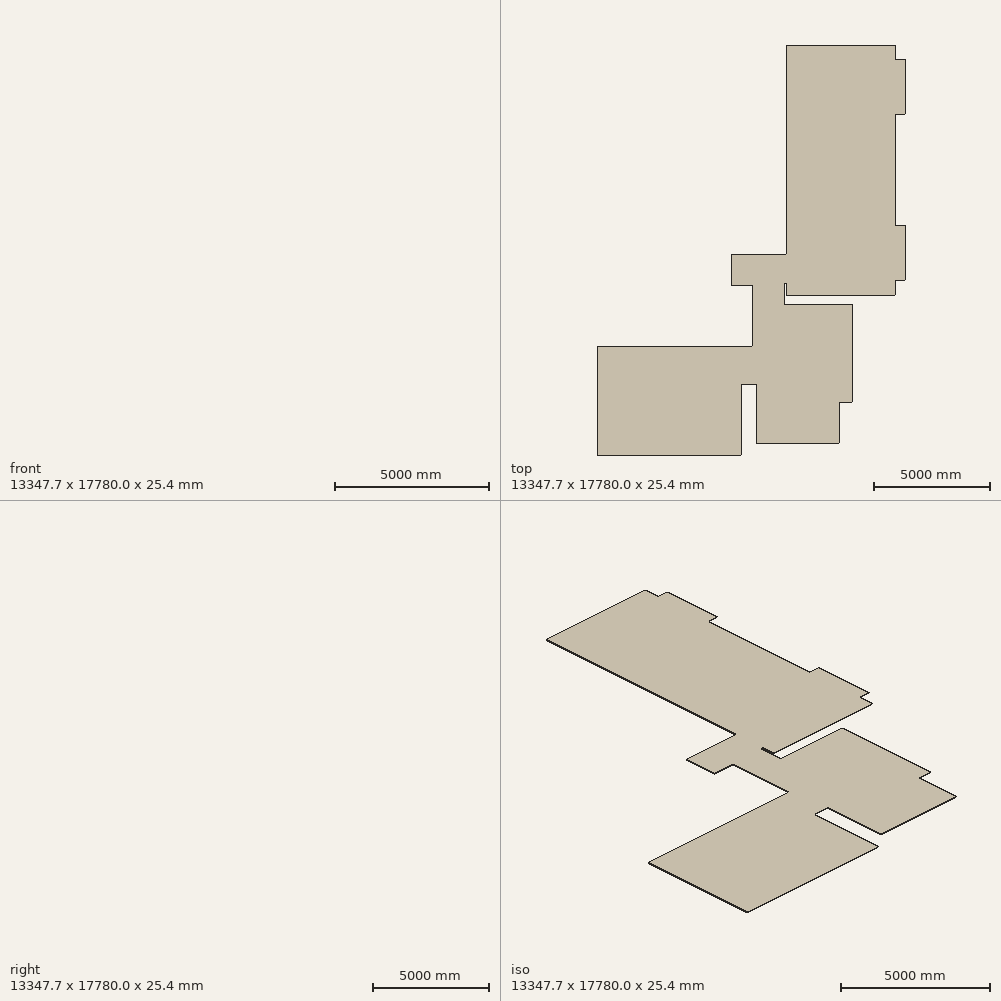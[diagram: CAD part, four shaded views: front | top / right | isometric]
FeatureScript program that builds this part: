
annotation { "Feature Type Name" : "Feature", "Feature Type Description" : "" }
export const myFeature = defineFeature(function(context is Context, id is Id, definition is map)
    precondition{}
    {
        {
            var Q0;
            Q0=qCreatedBy(makeId("Top.planeOp"),FACE);
            var sketch = newSketch(context, id + "F0", { "sketchPlane" : qUnion([Q0])});
            skLineSegment(sketch, "E0", {"start": v(0, 0) * mm, "end": v(6248.4, 0) * mm});
            skLineSegment(sketch, "E1", {"start": v(6248.4, 0) * mm, "end": v(6248.4, 3073.4) * mm});
            skLineSegment(sketch, "E2", {"start": v(6248.4, 3073.4) * mm, "end": v(6896.1, 3073.4) * mm});
            skLineSegment(sketch, "E3", {"start": v(6896.1, 3073.4) * mm, "end": v(6896.1, 533.4) * mm});
            skLineSegment(sketch, "E4", {"start": v(6896.1, 533.4) * mm, "end": v(10477.5, 533.4) * mm});
            skLineSegment(sketch, "E5", {"start": v(10477.5, 533.4) * mm, "end": v(10477.5, 2311.4) * mm});
            skLineSegment(sketch, "E6", {"start": v(10477.5, 2311.4) * mm, "end": v(11036.3, 2311.4) * mm});
            skLineSegment(sketch, "E7", {"start": v(11036.3, 2311.4) * mm, "end": v(11036.3, 6527.8) * mm});
            skLineSegment(sketch, "E8", {"start": v(11036.3, 6527.8) * mm, "end": v(8115.3, 6527.8) * mm});
            skLineSegment(sketch, "E9", {"start": v(8115.3, 6527.8) * mm, "end": v(8115.3, 7467.6) * mm});
            skLineSegment(sketch, "E10", {"start": v(8115.3, 7467.6) * mm, "end": v(8191.5, 7467.6) * mm});
            skLineSegment(sketch, "E11", {"start": v(8191.5, 7467.6) * mm, "end": v(8191.5, 6959.6) * mm});
            skLineSegment(sketch, "E12", {"start": v(8191.5, 6959.6) * mm, "end": v(12915.9, 6959.6) * mm});
            skLineSegment(sketch, "E13", {"start": v(12915.9, 6959.6) * mm, "end": v(12915.9, 7569.2) * mm});
            skLineSegment(sketch, "E14", {"start": v(12915.9, 7569.2) * mm, "end": v(13347.7, 7569.2) * mm});
            skLineSegment(sketch, "E15", {"start": v(13347.7, 7569.2) * mm, "end": v(13347.7, 9956.8) * mm});
            skLineSegment(sketch, "E16", {"start": v(13347.7, 9956.8) * mm, "end": v(12915.9, 9956.8) * mm});
            skLineSegment(sketch, "E17", {"start": v(12915.9, 9956.8) * mm, "end": v(12915.9, 14782.8) * mm});
            skLineSegment(sketch, "E18", {"start": v(12915.9, 14782.8) * mm, "end": v(13347.7, 14782.8) * mm});
            skLineSegment(sketch, "E19", {"start": v(13347.7, 14782.8) * mm, "end": v(13347.7, 17170.4) * mm});
            skLineSegment(sketch, "E20", {"start": v(13347.7, 17170.4) * mm, "end": v(12915.9, 17170.4) * mm});
            skLineSegment(sketch, "E21", {"start": v(12915.9, 17170.4) * mm, "end": v(12915.9, 17780) * mm});
            skLineSegment(sketch, "E22", {"start": v(12915.9, 17780) * mm, "end": v(8191.5, 17780) * mm});
            skLineSegment(sketch, "E23", {"start": v(8191.5, 8737.6) * mm, "end": v(8191.5, 17780) * mm});
            skLineSegment(sketch, "E24", {"start": v(0, 0) * mm, "end": v(0, 4724.4) * mm});
            skLineSegment(sketch, "E25", {"start": v(0, 4724.4) * mm, "end": v(6705.6, 4724.4) * mm});
            skLineSegment(sketch, "E26", {"start": v(6705.6, 4724.4) * mm, "end": v(6705.6, 7391.4) * mm});
            skLineSegment(sketch, "E27", {"start": v(6705.6, 7391.4) * mm, "end": v(5816.6, 7391.4) * mm});
            skLineSegment(sketch, "E28", {"start": v(5816.6, 7391.4) * mm, "end": v(5816.6, 8737.6) * mm});
            skLineSegment(sketch, "E29", {"start": v(5816.6, 8737.6) * mm, "end": v(8191.5, 8737.6) * mm});
            skSolve(sketch);
        }
        {
            var Q0;
            Q0=makeQuery(id+"F0.imprint","IMPRINT",FACE,{"disambiguationData":[TD([[makeQuery(id+"F0.imprint","IMPRINT",EDGE,{"derivedFrom":sQuery(id+"F0.wireOp",EDGE,"E0")}),1.0]])]});
            extrude(context, id + "F1", {"entities" : qUnion([Q0]), "depth" : 25.4 * mm, "offsetDistance" : 25.4 * mm});
        }
    });
